FCSTD DOCUMENT  (FreeCAD 0.18R16146 (Git))
Label: lp_hookah
License: All rights reserved
LicenseURL: http://en.wikipedia.org/wiki/All_rights_reserved
objects: Sketcher::SketchObject×1
note: 1 computed .brp shape members not serialized (recipe doc carries the construction recipe); baked Part::Feature solids carry a one-line shape summary decoded from their .brp

FEATURE [Sketcher::SketchObject] Sketch025
  MapMode = 2
  sketch-geometry (27):
    g0: LineSegment [constr] StartX=146.606 StartY=71.1613 StartZ=0 EndX=146.606 EndY=-11.3887 EndZ=0
    g1: LineSegment [constr] StartX=146.606 StartY=71.1613 StartZ=0 EndX=94.786 EndY=71.1613 EndZ=0
    g2: LineSegment [constr] StartX=94.786 StartY=71.1613 StartZ=0 EndX=94.786 EndY=73.4513 EndZ=0
    g3: LineSegment [constr] StartX=94.786 StartY=73.4513 StartZ=0 EndX=75.486 EndY=73.4513 EndZ=0
    g4: LineSegment [constr] StartX=75.486 StartY=73.4513 StartZ=0 EndX=75.486 EndY=79.5513 EndZ=0
    g5: LineSegment [constr] StartX=75.486 StartY=79.5513 StartZ=0 EndX=55.926 EndY=79.5513 EndZ=0
    g6: LineSegment [constr] StartX=55.926 StartY=79.5513 StartZ=0 EndX=55.926 EndY=74.4713 EndZ=0
    g7: LineSegment [constr] StartX=55.926 StartY=74.4713 StartZ=0 EndX=36.626 EndY=74.4713 EndZ=0
    g8: LineSegment [constr] StartX=36.626 StartY=74.4713 StartZ=0 EndX=36.626 EndY=63.2913 EndZ=0
    g9: LineSegment [constr] StartX=36.626 StartY=63.2913 StartZ=0 EndX=-6.46225 EndY=58.5344 EndZ=0
    g10: LineSegment [constr] StartX=-6.46225 StartY=58.5344 StartZ=0 EndX=0 EndY=0 EndZ=0
    g11: LineSegment [constr] StartX=0 StartY=0 StartZ=0 EndX=40.7524 EndY=4.49911 EndZ=0
    g12: LineSegment [constr] StartX=40.7524 StartY=4.49911 StartZ=0 EndX=40.0534 EndY=10.8306 EndZ=0
    g13: LineSegment [constr] StartX=40.0534 StartY=10.8306 StartZ=0 EndX=44.71 EndY=16.0571 EndZ=0
    g14: LineSegment [constr] StartX=44.71 StartY=16.0571 StartZ=0 EndX=84.6903 EndY=17.3135 EndZ=0
    g15: LineSegment [constr] StartX=84.6903 StartY=17.3135 StartZ=0 EndX=91.2207 EndY=13.8119 EndZ=0
    g16: LineSegment [constr] StartX=91.2207 StartY=13.8119 StartZ=0 EndX=92.1391 EndY=-4.96562 EndZ=0
    g17: LineSegment [constr] StartX=92.1391 StartY=-4.96562 StartZ=0 EndX=110.917 EndY=-4.04725 EndZ=0
    g18: LineSegment [constr] StartX=110.917 StartY=-4.04725 StartZ=0 EndX=127.829 EndY=-11.8616 EndZ=0
    g19: LineSegment [constr] StartX=127.829 StartY=-11.8616 StartZ=0 EndX=138.485 EndY=-26.3683 EndZ=0
    g20: LineSegment [constr] StartX=146.606 StartY=-11.3887 StartZ=0 EndX=151.717 EndY=-18.7969 EndZ=0
    g21: LineSegment [constr] StartX=151.717 StartY=-18.7969 StartZ=0 EndX=151.717 EndY=25.6285 EndZ=0
    g22: LineSegment [constr] StartX=151.717 StartY=-18.7969 StartZ=0 EndX=151.717 EndY=-2.67013 EndZ=0
    g23: LineSegment [constr] StartX=151.717 StartY=-18.7969 StartZ=0 EndX=151.188 EndY=-21.953 EndZ=0
    g24: LineSegment [constr] StartX=138.485 StartY=-26.3683 StartZ=0 EndX=88.829 EndY=-26.3683 EndZ=0
    g25: LineSegment [constr] StartX=138.485 StartY=-26.3683 StartZ=0 EndX=141.785 EndY=-26.1144 EndZ=0
    g26: LineSegment [constr] StartX=141.785 StartY=-26.1144 StartZ=0 EndX=151.188 EndY=-21.953 EndZ=0
  constraints (77):
    c: Vertical(g0)
    c: DistanceY(g0,g0) = 82.55
    c: Coincident(g1,g0)
    c: Horizontal(g1)
    c: DistanceX(g1,g1) = 51.82
    c: Coincident(g2,g1)
    c: Vertical(g2)
    c: DistanceY(g2,g2) = 2.29
    c: Coincident(g3,g2)
    c: Horizontal(g3)
    c: DistanceX(g3,g3) = 19.3
    c: Coincident(g4,g3)
    c: Vertical(g4)
    c: Coincident(g5,g4)
    c: Horizontal(g5)
    c: Vertical(g6)
    c: Horizontal(g7)
    c: Coincident(g8,g7)
    c: Vertical(g8)
    c: DistanceY(g4,g4) = 6.1
    c: DistanceY(g6,g6) = 5.08
    c: Coincident(g5,g6)
    c: Coincident(g6,g7)
    c: DistanceY(g8,g8) = 11.18
    c: DistanceX(g5,g5) = 19.56
    c: DistanceX(g7,g7) = 19.3
    c: Coincident(g9,g8)
    c: Angle(g8,g9) = 1.68075
    c: Distance(g9) = 43.35
    c: Coincident(g10,g9)
    c: Angle(g10,g9) = 1.5708
    c: Distance(g10) = 58.89
    c: Coincident(g11,g10)
    c: Angle(g11,g10) = 1.5708
    c: Distance(g11) = 41
    c: Coincident(g12,g11)
    c: Angle(g12,g11) = 1.5708
    c: Distance(g12) = 6.37
    c: Coincident(g13,g12)
    c: Angle(g12,g13) = 2.30383
    c: Distance(g13) = 7
    c: Coincident(g14,g13)
    c: Angle(g13,g14) = 2.33001
    c: Distance(g14) = 40
    c: Coincident(g15,g14)
    c: Coincident(g16,g15)
    c: Distance(g16) = 18.8
    c: Distance(g15) = 7.41
    c: Angle(g14,g15) = 2.61799
    c: Angle(g15,g16) = 2.11185
    c: Coincident(g17,g16)
    c: Angle(g17,g16) = 1.5708
    c: Distance(g17) = 18.8
    c: Coincident(g18,g17)
    c: Angle(g17,g18) = 2.65988
    c: Distance(g18) = 18.63
    c: Coincident(g19,g18)
    c: Distance(g19) = 18
    c: Angle(g18,g19) = 2.63719
    c: Coincident(g20,g0)
    c: Distance(g20) = 9
    c: Angle(g20,g0) = 2.53771
    c: Coincident(g21,g20)
    c: Vertical(g21)
    c: Coincident(g22,g20)
    c: Vertical(g22)
    c: Coincident(g23,g20)
    c: Angle(g23,g22) = 3.3074
    c: Distance(g23) = 3.2
    c: Coincident(g24,g19)
    c: Horizontal(g24)
    c: Coincident(g25,g19)
    c: Angle(g24,g25) = 3.21839
    c: Distance(g25) = 3.31
    c: Coincident(g26,g25)
    c: Coincident(g26,g23)
    c: Coincident(g10,g-1)
